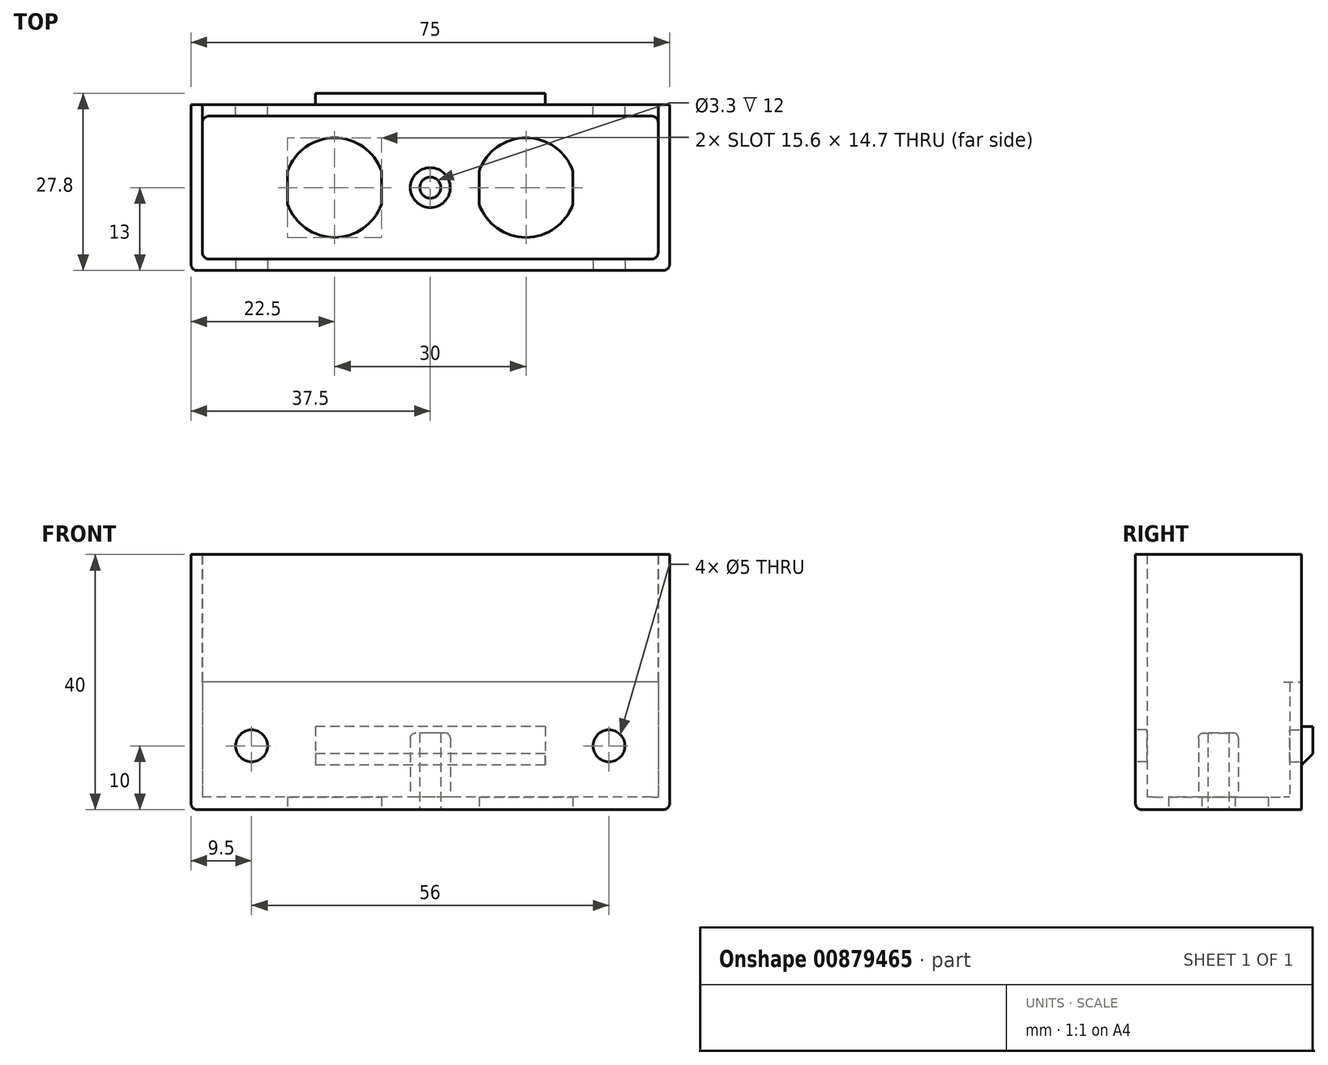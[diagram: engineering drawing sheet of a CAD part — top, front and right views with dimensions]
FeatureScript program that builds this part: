
annotation { "Feature Type Name" : "Feature", "Feature Type Description" : "" }
export const myFeature = defineFeature(function(context is Context, id is Id, definition is map)
    precondition{}
    {
        {
            var Q0;
            Q0=qCreatedBy(makeId("Top.planeOp"),FACE);
            var sketch = newSketch(context, id + "F0", { "sketchPlane" : qUnion([Q0])});
            skLineSegment(sketch, "E0.bottom", {"start": v(37.5, -13) * mm, "end": v(-37.5, -13) * mm});
            skLineSegment(sketch, "E0.top", {"start": v(37.5, 13) * mm, "end": v(-37.5, 13) * mm});
            skLineSegment(sketch, "E0.left", {"start": v(37.5, -13) * mm, "end": v(37.5, 13) * mm});
            skLineSegment(sketch, "E0.right", {"start": v(-37.5, -13) * mm, "end": v(-37.5, 13) * mm});
            skPoint(sketch, "E0.middle", {"position": v(0, 0) * mm});
            skSolve(sketch);
        }
        {
            var Q0;
            Q0 = qSketchRegion(id + "F0", true);
            extrude(context, id + "F1", {"entities" : qUnion([Q0]), "depth" : 2 * mm, "offsetDistance" : 25 * mm});
        }
        {
            var Q0;
            Q0=makeQuery(id+"F1.opExtrude","CAP_FACE",FACE,{"disambiguationData":[OSD([sQuery(id+"F0.wireOp",EDGE,"E0.bottom"),sQuery(id+"F0.wireOp",EDGE,"E0.top"),sQuery(id+"F0.wireOp",EDGE,"E0.left"),sQuery(id+"F0.wireOp",EDGE,"E0.right")])],"isStart":false});
            var sketch = newSketch(context, id + "F2", { "sketchPlane" : qUnion([Q0])});
            skLineSegment(sketch, "E1.bottom", {"start": v(35.7, -11.2) * mm, "end": v(-35.7, -11.2) * mm});
            skLineSegment(sketch, "E1.top", {"start": v(35.7, 11.2) * mm, "end": v(-35.7, 11.2) * mm});
            skLineSegment(sketch, "E1.left", {"start": v(35.7, -11.2) * mm, "end": v(35.7, 11.2) * mm});
            skLineSegment(sketch, "E1.right", {"start": v(-35.7, -11.2) * mm, "end": v(-35.7, 11.2) * mm});
            skPoint(sketch, "E1.middle", {"position": v(0, 0) * mm});
            skLineSegment(sketch, "E2.bottom", {"start": v(37.5, -13) * mm, "end": v(-37.5, -13) * mm});
            skLineSegment(sketch, "E2.top", {"start": v(37.5, 13) * mm, "end": v(-37.5, 13) * mm});
            skLineSegment(sketch, "E2.left", {"start": v(37.5, -13) * mm, "end": v(37.5, 13) * mm});
            skLineSegment(sketch, "E2.right", {"start": v(-37.5, -13) * mm, "end": v(-37.5, 13) * mm});
            skSolve(sketch);
        }
        {
            var Q0;
            Q0 = qSketchRegion(id + "F2", true);
            extrude(context, id + "F3", {"entities" : qUnion([Q0]), "operationType" : NewBodyOperationType.ADD, "depth" : 38 * mm, "offsetDistance" : 25 * mm});
        }
        {
            var Q0;
            Q0=makeQuery(id+"F1.opExtrude","CAP_FACE",FACE,{"disambiguationData":[OSD([sQuery(id+"F0.wireOp",EDGE,"E0.bottom"),sQuery(id+"F0.wireOp",EDGE,"E0.top"),sQuery(id+"F0.wireOp",EDGE,"E0.left"),sQuery(id+"F0.wireOp",EDGE,"E0.right")])],"isStart":true});
            var sketch = newSketch(context, id + "F4", { "sketchPlane" : qUnion([Q0])});
            skArc(sketch, "E3", {"start": v(-22.35, -2.61) * mm, "mid": v(-15, -7.8) * mm, "end": v(-7.65, -2.61) * mm});
            skLineSegment(sketch, "E4.left", {"start": v(-22.35, 2.61) * mm, "end": v(-22.35, -2.61) * mm});
            skLineSegment(sketch, "E4.right", {"start": v(-7.65, 2.61) * mm, "end": v(-7.65, -2.61) * mm});
            skArc(sketch, "E5.trimOffspring", {"start": v(-7.65, 2.61) * mm, "mid": v(-15, 7.8) * mm, "end": v(-22.35, 2.61) * mm});
            skLineSegment(sketch, "E6", {"start": v(0, 27.64) * mm, "end": v(0, -27.17) * mm, "construction": true});
            skArc(sketch, "E7.MirrorCS", {"start": v(7.65, 2.61) * mm, "mid": v(15, 7.8) * mm, "end": v(22.35, 2.61) * mm});
            skArc(sketch, "E8.MirrorCS", {"start": v(22.35, -2.61) * mm, "mid": v(15, -7.8) * mm, "end": v(7.65, -2.61) * mm});
            skLineSegment(sketch, "E9.MirrorCS", {"start": v(7.65, 2.61) * mm, "end": v(7.65, -2.61) * mm});
            skLineSegment(sketch, "E10.MirrorCS", {"start": v(22.35, 2.61) * mm, "end": v(22.35, -2.61) * mm});
            skSolve(sketch);
        }
        {
            var Q0;
            Q0 = qSketchRegion(id + "F4", true);
            extrude(context, id + "F5", {"entities" : qUnion([Q0]), "operationType" : NewBodyOperationType.REMOVE, "endBound" : BoundingType.UP_TO_NEXT, "oppositeDirection" : true, "depth" : 25 * mm, "offsetDistance" : 25 * mm});
        }
        {
            var Q0;
            Q0=makeQuery(id+"F3.boolean.opBoolean","MERGE",FACE,{"derivedFrom":[makeQuery(id+"F1.opExtrude","SWEPT_FACE",FACE,{"disambiguationData":[OSD([sQuery(id+"F0.wireOp",EDGE,"E0.top")])]}),makeQuery(id+"F3.opExtrude","SWEPT_FACE",FACE,{"disambiguationData":[OSD([sQuery(id+"F2.wireOp",EDGE,"E2.top")])]})]});
            var sketch = newSketch(context, id + "F6", { "sketchPlane" : qUnion([Q0])});
            skCircle(sketch, "E11", {"center": v(28, 10) * mm, "radius": 2.5 * mm});
            skCircle(sketch, "E12", {"center": v(-28, 10) * mm, "radius": 2.5 * mm});
            skSolve(sketch);
        }
        {
            var Q0;
            Q0 = qSketchRegion(id + "F6", true);
            extrude(context, id + "F7", {"entities" : qUnion([Q0]), "operationType" : NewBodyOperationType.REMOVE, "endBound" : BoundingType.UP_TO_NEXT, "oppositeDirection" : true, "depth" : 25 * mm, "offsetDistance" : 25 * mm});
        }
        {
            var Q0;
            Q0=makeQuery(id+"F3.boolean.opBoolean","MERGE",FACE,{"derivedFrom":[makeQuery(id+"F1.opExtrude","SWEPT_FACE",FACE,{"disambiguationData":[OSD([sQuery(id+"F0.wireOp",EDGE,"E0.top")])]}),makeQuery(id+"F3.opExtrude","SWEPT_FACE",FACE,{"disambiguationData":[OSD([sQuery(id+"F2.wireOp",EDGE,"E2.top")])]})]});
            var sketch = newSketch(context, id + "F8", { "sketchPlane" : qUnion([Q0])});
            skLineSegment(sketch, "E13.bottom", {"start": v(-18, 13) * mm, "end": v(18, 13) * mm});
            skLineSegment(sketch, "E13.top", {"start": v(-18, 7) * mm, "end": v(18, 7) * mm});
            skLineSegment(sketch, "E13.left", {"start": v(-18, 13) * mm, "end": v(-18, 7) * mm});
            skLineSegment(sketch, "E13.right", {"start": v(18, 13) * mm, "end": v(18, 7) * mm});
            skPoint(sketch, "E13.middle", {"position": v(0, 10) * mm});
            skSolve(sketch);
        }
        {
            var Q0;
            Q0 = qSketchRegion(id + "F8", true);
            extrude(context, id + "F9", {"entities" : qUnion([Q0]), "operationType" : NewBodyOperationType.ADD, "depth" : 1.8 * mm, "offsetDistance" : 25 * mm});
        }
        {
            var Q0;
            Q0=makeQuery(id+"F9.opExtrude","CAP_EDGE",EDGE,{"disambiguationData":[OSD([sQuery(id+"F8.wireOp",EDGE,"E13.top")])],"isStart":false});
            chamfer(context, id + "F10", {"entities" : qUnion([Q0]), "width" : 1.8 * mm, "tangentPropagation" : true});
        }
        {
            var Q0;
            Q0=makeQuery(id+"F3.opExtrude","CAP_FACE",FACE,{"disambiguationData":[OSD([sQuery(id+"F2.wireOp",EDGE,"E1.bottom"),sQuery(id+"F2.wireOp",EDGE,"E1.top"),sQuery(id+"F2.wireOp",EDGE,"E1.left"),sQuery(id+"F2.wireOp",EDGE,"E1.right"),sQuery(id+"F2.wireOp",EDGE,"E2.bottom"),sQuery(id+"F2.wireOp",EDGE,"E2.top"),sQuery(id+"F2.wireOp",EDGE,"E2.left"),sQuery(id+"F2.wireOp",EDGE,"E2.right")])],"isStart":false});
            var sketch = newSketch(context, id + "F11", { "sketchPlane" : qUnion([Q0])});
            skLineSegment(sketch, "E14.bottom", {"start": v(35.7, 11.2) * mm, "end": v(-35.7, 11.2) * mm});
            skLineSegment(sketch, "E14.top", {"start": v(35.7, 13) * mm, "end": v(-35.7, 13) * mm});
            skLineSegment(sketch, "E14.left", {"start": v(35.7, 11.2) * mm, "end": v(35.7, 13) * mm});
            skLineSegment(sketch, "E14.right", {"start": v(-35.7, 11.2) * mm, "end": v(-35.7, 13) * mm});
            skSolve(sketch);
        }
        {
            var Q0;
            Q0 = qSketchRegion(id + "F11", true);
            extrude(context, id + "F12", {"entities" : qUnion([Q0]), "operationType" : NewBodyOperationType.REMOVE, "oppositeDirection" : true, "depth" : 20 * mm, "offsetDistance" : 25 * mm});
        }
        {
            var Q0;
            Q0=makeQuery(id+"F1.opExtrude","CAP_FACE",FACE,{"disambiguationData":[OSD([sQuery(id+"F0.wireOp",EDGE,"E0.bottom"),sQuery(id+"F0.wireOp",EDGE,"E0.top"),sQuery(id+"F0.wireOp",EDGE,"E0.left"),sQuery(id+"F0.wireOp",EDGE,"E0.right")])],"isStart":false});
            var sketch = newSketch(context, id + "F13", { "sketchPlane" : qUnion([Q0])});
            skCircle(sketch, "E15", {"center": v(0, 0) * mm, "radius": 3.12 * mm});
            skSolve(sketch);
        }
        {
            var Q0;
            Q0 = qSketchRegion(id + "F13", true);
            extrude(context, id + "F14", {"entities" : qUnion([Q0]), "operationType" : NewBodyOperationType.ADD, "depth" : 10 * mm, "offsetDistance" : 25 * mm});
        }
        {
            var Q0;
            Q0=makeQuery(id+"F14.opExtrude","CAP_EDGE",EDGE,{"disambiguationData":[OSD([sQuery(id+"F13.wireOp",EDGE,"E15")])],"isStart":false});
            fillet(context, id + "F15", {"entities" : qUnion([Q0]), "radius" : 0.75 * mm, "tangentPropagation" : true, "allowEdgeOverflow" : false});
        }
        {
            var Q0;
            Q0=makeQuery(id+"F4.imprint","IMPRINT",FACE,{"disambiguationData":[TD([[makeQuery(id+"F4.imprint","IMPRINT",EDGE,{"derivedFrom":sQuery(id+"F4.wireOp",EDGE,"E3")}),-1.0]])]});
            var sketch = newSketch(context, id + "F16", { "sketchPlane" : qUnion([Q0])});
            skCircle(sketch, "E16", {"center": v(0, 0) * mm, "radius": 1.65 * mm});
            skSolve(sketch);
        }
        {
            var Q0;
            Q0 = qSketchRegion(id + "F16", true);
            extrude(context, id + "F17", {"entities" : qUnion([Q0]), "operationType" : NewBodyOperationType.REMOVE, "endBound" : BoundingType.THROUGH_ALL, "oppositeDirection" : true, "depth" : 25 * mm, "offsetDistance" : 25 * mm});
        }
        {
            var Q0;
            Q0=makeQuery(id+"F3.boolean.opBoolean","MERGE",EDGE,{"derivedFrom":[makeQuery(id+"F1.opExtrude","SWEPT_EDGE",EDGE,{"disambiguationData":[OSD([sQuery(id+"F0.wireOp",EDGE,"E0.bottom"),sQuery(id+"F0.wireOp",EDGE,"E0.right")])]}),makeQuery(id+"F3.opExtrude","SWEPT_EDGE",EDGE,{"disambiguationData":[OSD([sQuery(id+"F2.wireOp",EDGE,"E2.bottom"),sQuery(id+"F2.wireOp",EDGE,"E2.right")])]})]});
            var Q1;
            Q1=makeQuery(id+"F3.boolean.opBoolean","MERGE",EDGE,{"derivedFrom":[makeQuery(id+"F1.opExtrude","SWEPT_EDGE",EDGE,{"disambiguationData":[OSD([sQuery(id+"F0.wireOp",EDGE,"E0.bottom"),sQuery(id+"F0.wireOp",EDGE,"E0.left")])]}),makeQuery(id+"F3.opExtrude","SWEPT_EDGE",EDGE,{"disambiguationData":[OSD([sQuery(id+"F2.wireOp",EDGE,"E2.bottom"),sQuery(id+"F2.wireOp",EDGE,"E2.left")])]})]});
            var Q2;
            Q2=makeQuery(id+"F3.opExtrude","SWEPT_EDGE",EDGE,{"disambiguationData":[OSD([sQuery(id+"F2.wireOp",EDGE,"E1.bottom"),sQuery(id+"F2.wireOp",EDGE,"E1.right")])]});
            var Q3;
            Q3=makeQuery(id+"F3.opExtrude","SWEPT_EDGE",EDGE,{"disambiguationData":[OSD([sQuery(id+"F2.wireOp",EDGE,"E1.bottom"),sQuery(id+"F2.wireOp",EDGE,"E1.left")])]});
            var Q4;
            Q4=makeQuery(id+"F3.opExtrude","CAP_EDGE",EDGE,{"disambiguationData":[OSD([sQuery(id+"F2.wireOp",EDGE,"E1.bottom")])],"isStart":true});
            var Q5;
            Q5=makeQuery(id+"F3.opExtrude","CAP_EDGE",EDGE,{"disambiguationData":[OSD([sQuery(id+"F2.wireOp",EDGE,"E1.left")])],"isStart":true});
            var Q6;
            Q6=makeQuery(id+"F3.opExtrude","CAP_EDGE",EDGE,{"disambiguationData":[OSD([sQuery(id+"F2.wireOp",EDGE,"E1.right")])],"isStart":true});
            var Q7;
            Q7=makeQuery(id+"F1.opExtrude","CAP_EDGE",EDGE,{"disambiguationData":[OSD([sQuery(id+"F0.wireOp",EDGE,"E0.bottom")])],"isStart":true});
            var Q8;
            Q8=makeQuery(id+"F1.opExtrude","CAP_EDGE",EDGE,{"disambiguationData":[OSD([sQuery(id+"F0.wireOp",EDGE,"E0.left")])],"isStart":true});
            var Q9;
            Q9=makeQuery(id+"F1.opExtrude","CAP_EDGE",EDGE,{"disambiguationData":[OSD([sQuery(id+"F0.wireOp",EDGE,"E0.right")])],"isStart":true});
            var Q10;
            Q10=makeQuery(id+"F3.opExtrude","CAP_EDGE",EDGE,{"disambiguationData":[OSD([sQuery(id+"F2.wireOp",EDGE,"E1.top")])],"isStart":true});
            var Q11;
            Q11=makeQuery(id+"F3.opExtrude","SWEPT_EDGE",EDGE,{"disambiguationData":[OSD([sQuery(id+"F2.wireOp",EDGE,"E1.top"),sQuery(id+"F2.wireOp",EDGE,"E1.left")])]});
            var Q12;
            Q12=makeQuery(id+"F3.opExtrude","SWEPT_EDGE",EDGE,{"disambiguationData":[OSD([sQuery(id+"F2.wireOp",EDGE,"E1.top"),sQuery(id+"F2.wireOp",EDGE,"E1.right")])]});
            var Q13;
            Q13=makeQuery(id+"F12.boolean.opBoolean","COPY",EDGE,{"derivedFrom":makeQuery(id+"F12.opExtrude","CAP_EDGE",EDGE,{"disambiguationData":[OSD([sQuery(id+"F11.wireOp",EDGE,"E14.bottom")])],"isStart":false})});
            fillet(context, id + "F18", {"entities" : qUnion([Q0, Q1, Q2, Q3, Q4, Q5, Q6, Q7, Q8, Q9, Q10, Q11, Q12, Q13]), "radius" : 1 * mm, "tangentPropagation" : true, "allowEdgeOverflow" : false});
        }
        {
            var Q0;
            Q0=makeQuery(id+"F3.boolean.opBoolean","MERGE",FACE,{"derivedFrom":[makeQuery(id+"F1.opExtrude","SWEPT_FACE",FACE,{"disambiguationData":[OSD([sQuery(id+"F0.wireOp",EDGE,"E0.bottom")])]}),makeQuery(id+"F3.opExtrude","SWEPT_FACE",FACE,{"disambiguationData":[OSD([sQuery(id+"F2.wireOp",EDGE,"E2.bottom")])]})]});
            var sketch = newSketch(context, id + "F19", { "sketchPlane" : qUnion([Q0])});
            skCircle(sketch, "E17", {"center": v(28, 10) * mm, "radius": 2.5 * mm});
            skCircle(sketch, "E18", {"center": v(-28, 10) * mm, "radius": 2.5 * mm});
            skSolve(sketch);
        }
        {
            var Q0;
            Q0 = qSketchRegion(id + "F19", true);
            extrude(context, id + "F20", {"entities" : qUnion([Q0]), "operationType" : NewBodyOperationType.REMOVE, "endBound" : BoundingType.THROUGH_ALL, "oppositeDirection" : true, "depth" : 25 * mm, "offsetDistance" : 25 * mm});
        }
    });
